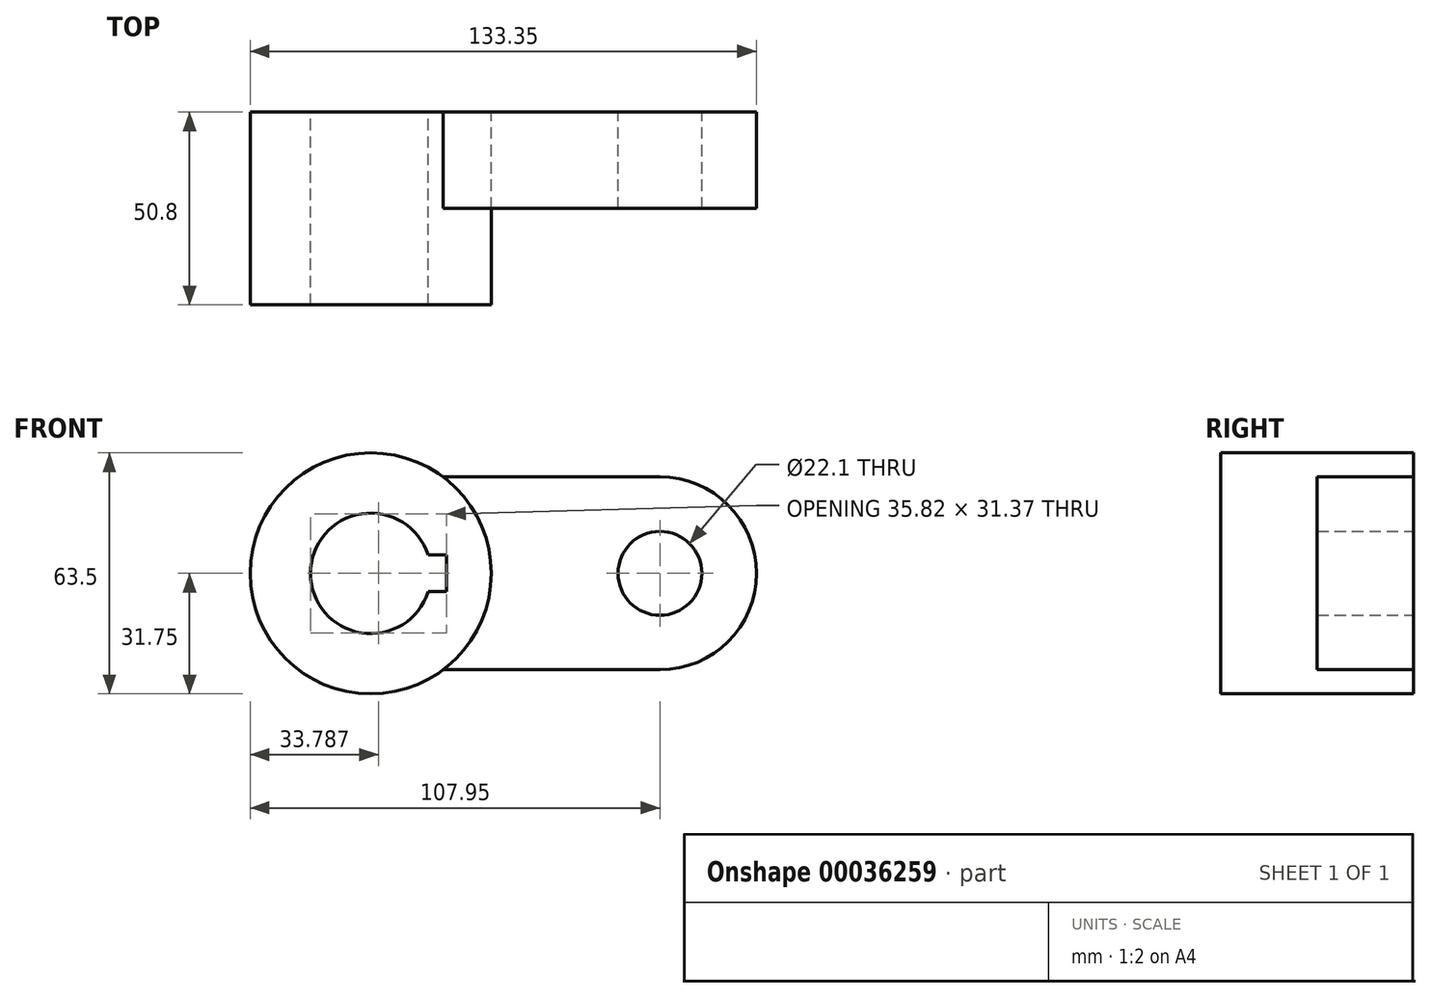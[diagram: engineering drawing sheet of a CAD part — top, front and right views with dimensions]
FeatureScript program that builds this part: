
annotation { "Feature Type Name" : "Feature", "Feature Type Description" : "" }
export const myFeature = defineFeature(function(context is Context, id is Id, definition is map)
    precondition{}
    {
        {
            var Q0;
            Q0=qCreatedBy(makeId("Front.planeOp"),FACE);
            var sketch = newSketch(context, id + "F0", { "sketchPlane" : qUnion([Q0])});
            skCircle(sketch, "E0", {"center": v(0, 0) * mm, "radius": 31.75 * mm});
            skCircle(sketch, "E1", {"center": v(76.2, 0) * mm, "radius": 25.4 * mm});
            skCircle(sketch, "E2", {"center": v(76.2, 0) * mm, "radius": 11.05 * mm});
            skLineSegment(sketch, "E3", {"start": v(76.2, 25.4) * mm, "end": v(19.05, 25.4) * mm});
            skCircle(sketch, "E4", {"center": v(0, 0) * mm, "radius": 15.88 * mm});
            skLineSegment(sketch, "E5", {"start": v(76.2, -25.4) * mm, "end": v(19.05, -25.4) * mm});
            skLineSegment(sketch, "E6", {"start": v(19.95, 4.83) * mm, "end": v(15.12, 4.83) * mm});
            skLineSegment(sketch, "E7.MirrorCS", {"start": v(19.95, -4.83) * mm, "end": v(15.12, -4.83) * mm});
            skLineSegment(sketch, "E8", {"start": v(19.95, 4.83) * mm, "end": v(19.95, -4.83) * mm});
            skSolve(sketch);
        }
        {
            var Q0;
            Q0=makeQuery(id+"F0.imprint","IMPRINT",FACE,{"disambiguationData":[TD([[makeQuery(id+"F0.imprint","IMPRINT",EDGE,{"derivedFrom":sQuery(id+"F0.wireOp",EDGE,"E2")}),-1.0]])]});
            var Q1;
            {var subQ1=sQuery(id+"F0.wireOp",EDGE,"E3");Q1=makeQuery(id+"F0.imprint","IMPRINT",FACE,{"disambiguationData":[TD([[makeQuery(id+"F0.imprint","IMPRINT",EDGE,{"derivedFrom":subQ1}),1.0]])]});}
            extrude(context, id + "F1", {"entities" : qUnion([Q0, Q1]), "depth" : 25.4 * mm});
        }
        {
            var Q0;
            Q0 = qSketchRegion(id + "FGEZsctJK6WnKtq_1", true);
            var Q1;
            {var subQ1=sQuery(id+"F0.wireOp",EDGE,"E6");Q1=makeQuery(id+"F0.imprint","IMPRINT",FACE,{"disambiguationData":[TD([[makeQuery(id+"F0.imprint","IMPRINT",EDGE,{"derivedFrom":subQ1}),-1.0]])]});}
            extrude(context, id + "F2", {"entities" : qUnion([Q0, Q1]), "depth" : 50.8 * mm});
        }
    });
